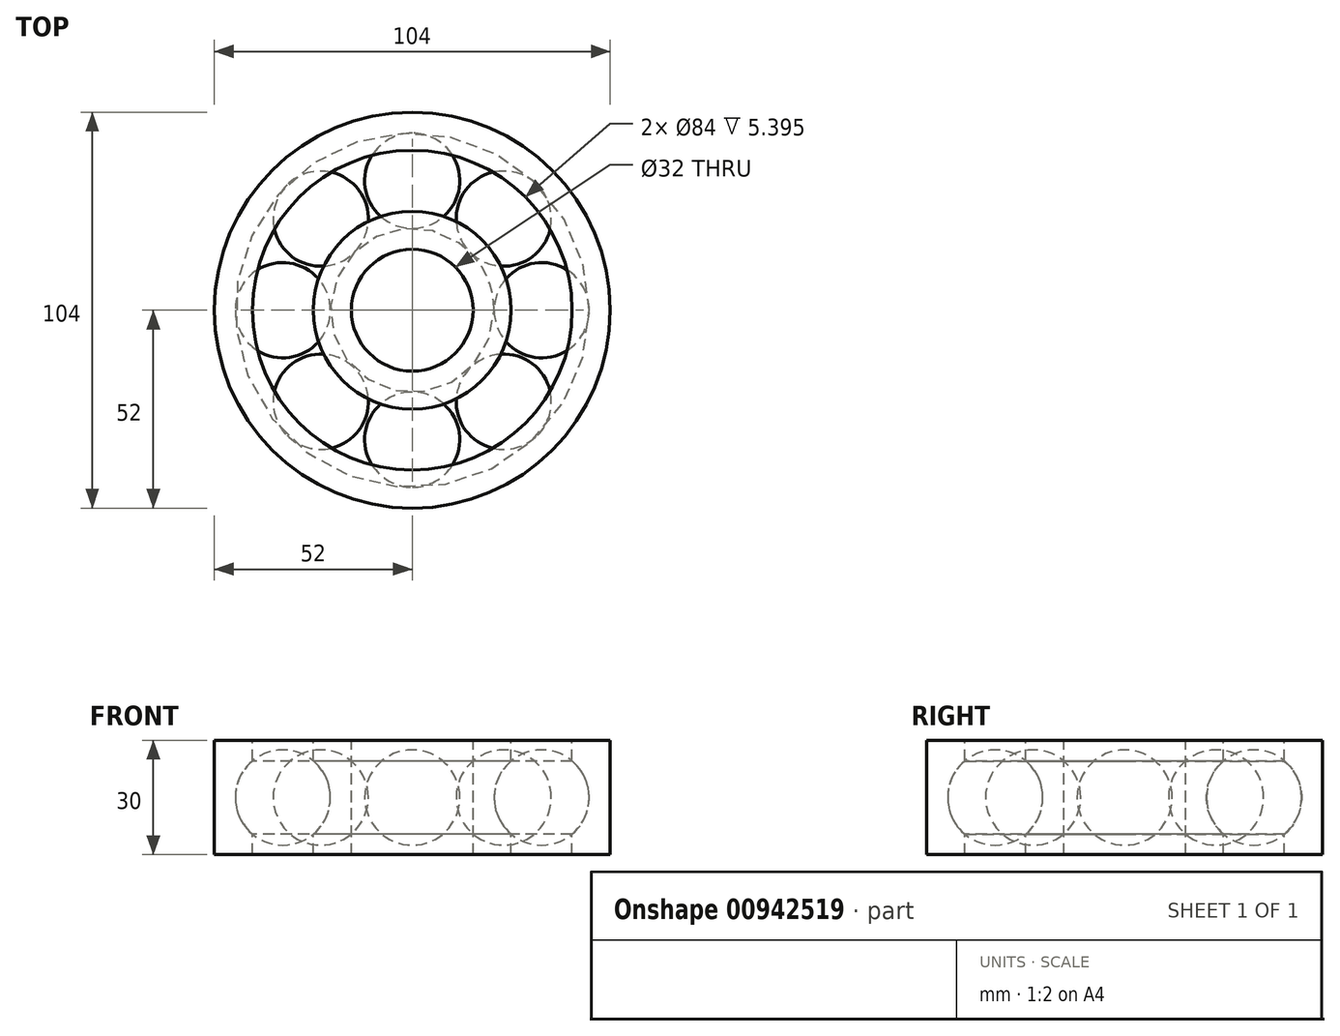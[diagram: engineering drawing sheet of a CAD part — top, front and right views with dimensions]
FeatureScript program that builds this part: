
annotation { "Feature Type Name" : "Feature", "Feature Type Description" : "" }
export const myFeature = defineFeature(function(context is Context, id is Id, definition is map)
    precondition{}
    {
        {
            var Q0;
            Q0=qCreatedBy(makeId("Front.planeOp"),FACE);
            var sketch = newSketch(context, id + "F0", { "sketchPlane" : qUnion([Q0])});
            skLineSegment(sketch, "E0", {"start": v(0, 33.18) * mm, "end": v(0, 0) * mm, "construction": true});
            skLineSegment(sketch, "E1", {"start": v(0, 0) * mm, "end": v(91.02, 0) * mm, "construction": true});
            skCircle(sketch, "E2", {"center": v(34, 0) * mm, "radius": 12.5 * mm});
            skLineSegment(sketch, "E3", {"start": v(26, 9.6) * mm, "end": v(26, 15) * mm});
            skLineSegment(sketch, "E4", {"start": v(26, 15) * mm, "end": v(16, 15) * mm});
            skLineSegment(sketch, "E5", {"start": v(16, 15) * mm, "end": v(16, -15) * mm});
            skLineSegment(sketch, "E6", {"start": v(16, -15) * mm, "end": v(26, -15) * mm});
            skLineSegment(sketch, "E7", {"start": v(26, -15) * mm, "end": v(26, -9.6) * mm});
            skLineSegment(sketch, "E8", {"start": v(42, 9.6) * mm, "end": v(42, 15) * mm});
            skLineSegment(sketch, "E9", {"start": v(42, 15) * mm, "end": v(52, 15) * mm});
            skLineSegment(sketch, "E10", {"start": v(52, 15) * mm, "end": v(52, -15) * mm});
            skLineSegment(sketch, "E11", {"start": v(52, -15) * mm, "end": v(42, -15) * mm});
            skLineSegment(sketch, "E12", {"start": v(42, -15) * mm, "end": v(42, -9.6) * mm});
            skLineSegment(sketch, "E13", {"start": v(21.5, 0) * mm, "end": v(46.5, 0) * mm});
            skLineSegment(sketch, "E14", {"start": v(16, 0) * mm, "end": v(21.5, 0) * mm});
            skLineSegment(sketch, "E15", {"start": v(46.5, 0) * mm, "end": v(52, 0) * mm});
            skLineSegment(sketch, "E16", {"start": v(0, 33.18) * mm, "end": v(0, -30) * mm});
            skSolve(sketch);
        }
        {
            var Q0;
            {var subQ2=sQuery(id+"F0.wireOp",EDGE,"E13");Q0=makeQuery(id+"F0.imprint","IMPRINT",FACE,{"disambiguationData":[TD([[makeQuery(id+"F0.imprint","IMPRINT",EDGE,{"derivedFrom":subQ2}),1.0]])]});}
            var Q1;
            Q1=sQuery(id+"F0.wireOp",EDGE,"E13");
            revolve(context, id + "F1", {"surfaceOperationType" : NewSurfaceOperationType.NEW, "entities" : qUnion([Q0]), "axis" : qUnion([Q1]), "revolveType" : RevolveType.FULL});
        }
        {
            var Q0;
            {var subQ1=sQuery(id+"F0.wireOp",EDGE,"E6");Q0=makeQuery(id+"F0.imprint","IMPRINT",FACE,{"disambiguationData":[TD([[makeQuery(id+"F0.imprint","IMPRINT",EDGE,{"derivedFrom":subQ1}),1.0]])]});}
            var Q1;
            {var subQ3=sQuery(id+"F0.wireOp",EDGE,"E3");Q1=makeQuery(id+"F0.imprint","IMPRINT",FACE,{"disambiguationData":[TD([[makeQuery(id+"F0.imprint","IMPRINT",EDGE,{"derivedFrom":subQ3}),1.0]])]});}
            var Q2;
            Q2=sQuery(id+"F0.wireOp",EDGE,"E16");
            revolve(context, id + "F2", {"surfaceOperationType" : NewSurfaceOperationType.NEW, "entities" : qUnion([Q0, Q1]), "axis" : qUnion([Q2]), "revolveType" : RevolveType.FULL});
        }
        {
            var Q0;
            {var subQ3=sQuery(id+"F0.wireOp",EDGE,"E8");Q0=makeQuery(id+"F0.imprint","IMPRINT",FACE,{"disambiguationData":[TD([[makeQuery(id+"F0.imprint","IMPRINT",EDGE,{"derivedFrom":subQ3}),-1.0]])]});}
            var Q1;
            {var subQ1=sQuery(id+"F0.wireOp",EDGE,"E11");Q1=makeQuery(id+"F0.imprint","IMPRINT",FACE,{"disambiguationData":[TD([[makeQuery(id+"F0.imprint","IMPRINT",EDGE,{"derivedFrom":subQ1}),-1.0]])]});}
            var Q2;
            Q2=sQuery(id+"F0.wireOp",EDGE,"E16");
            revolve(context, id + "F3", {"surfaceOperationType" : NewSurfaceOperationType.NEW, "entities" : qUnion([Q0, Q1]), "axis" : qUnion([Q2]), "revolveType" : RevolveType.FULL});
        }
        {
            var Q0;
            Q0=makeQuery(id+"F1.opRevolve","SWEPT_BODY",BODY,{"disambiguationData":[OSD([sQuery(id+"F0.wireOp",EDGE,"E2"),sQuery(id+"F0.wireOp",EDGE,"E13")])]});
            var Q1;
            Q1=sQuery(id+"F0.wireOp",EDGE,"E16");
            circularPattern(context, id + "F4", {"entities" : qUnion([Q0]), "axis" : qUnion([Q1]), "angle" : 360 * degree, "instanceCount" : 8, "equalSpace" : true});
        }
    });
